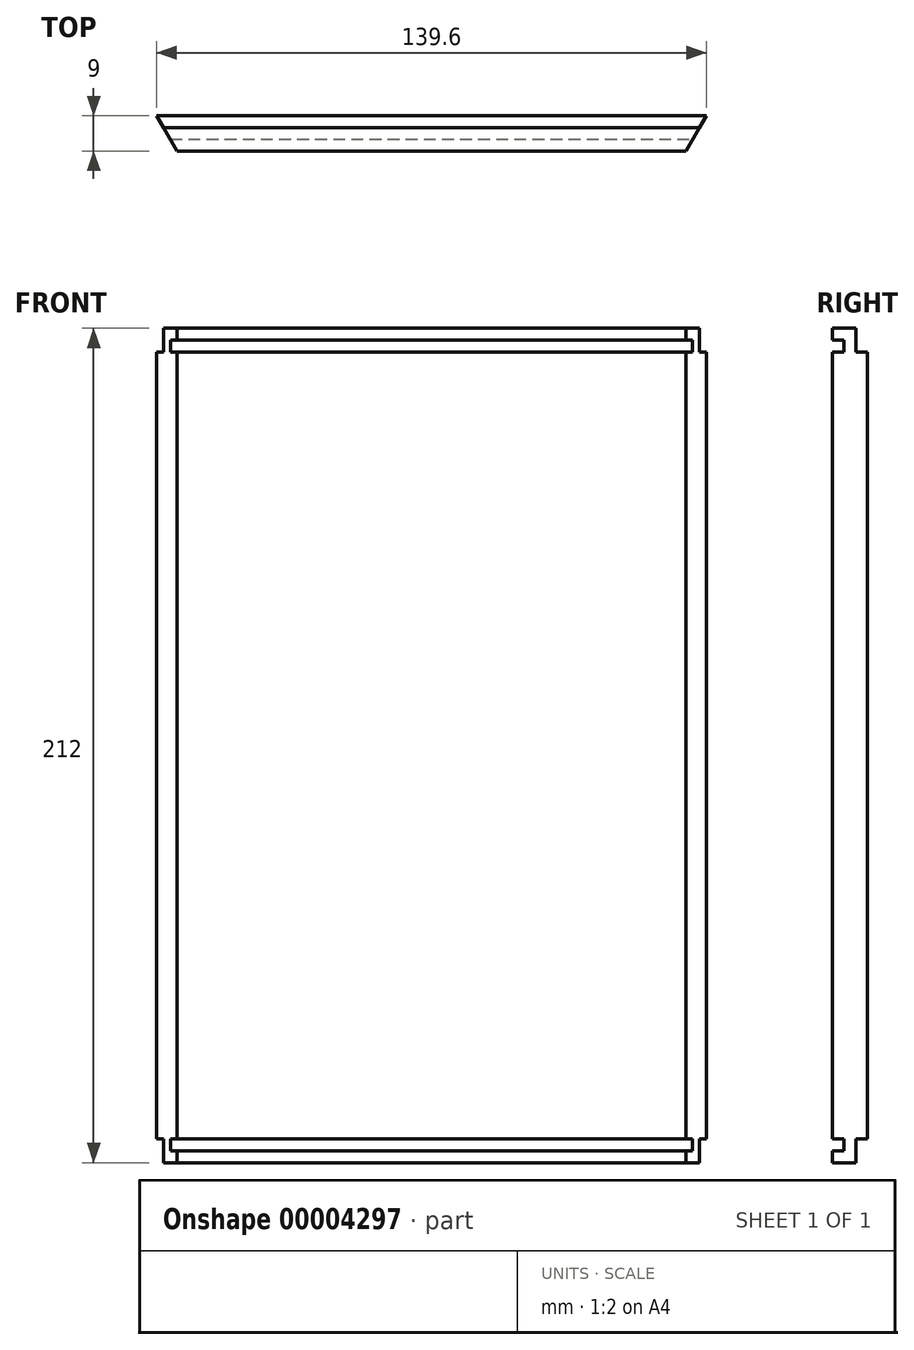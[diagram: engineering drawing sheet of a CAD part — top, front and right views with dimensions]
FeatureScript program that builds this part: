
annotation { "Feature Type Name" : "Feature", "Feature Type Description" : "" }
export const myFeature = defineFeature(function(context is Context, id is Id, definition is map)
    precondition{}
    {
        {
            var Q0;
            Q0=qCreatedBy(makeId("Front.planeOp"),FACE);
            var sketch = newSketch(context, id + "F0", { "sketchPlane" : qUnion([Q0])});
            skLineSegment(sketch, "E0.bottom", {"start": v(-52.97, 148.92) * mm, "end": v(97.03, 148.92) * mm});
            skLineSegment(sketch, "E0.top", {"start": v(-52.97, -51.08) * mm, "end": v(97.03, -51.08) * mm});
            skLineSegment(sketch, "E0.left", {"start": v(-52.97, 148.92) * mm, "end": v(-52.97, -51.08) * mm});
            skLineSegment(sketch, "E0.right", {"start": v(97.03, 148.92) * mm, "end": v(97.03, -51.08) * mm});
            skSolve(sketch);
        }
        {
            var Q0;
            Q0=makeQuery(id+"F0.imprint","IMPRINT",FACE,{"disambiguationData":[TD([[makeQuery(id+"F0.imprint","IMPRINT",EDGE,{"derivedFrom":sQuery(id+"F0.wireOp",EDGE,"E0.bottom")}),-1.0]])]});
            extrude(context, id + "F1", {"entities" : qUnion([Q0]), "depth" : 9 * mm});
        }
        {
            var Q0;
            Q0=makeQuery(id+"F1.opExtrude","SWEPT_FACE",FACE,{"disambiguationData":[OSD([sQuery(id+"F0.wireOp",EDGE,"E0.bottom")])]});
            var sketch = newSketch(context, id + "F2", { "sketchPlane" : qUnion([Q0])});
            skLineSegment(sketch, "E1", {"start": v(-52.97, 0) * mm, "end": v(-52.97, -9) * mm});
            skLineSegment(sketch, "E2", {"start": v(-52.97, -9) * mm, "end": v(97.03, -9) * mm});
            skLineSegment(sketch, "E3", {"start": v(97.03, -9) * mm, "end": v(97.03, 0) * mm});
            skLineSegment(sketch, "E4", {"start": v(97.03, 0) * mm, "end": v(-52.97, 0) * mm});
            skLineSegment(sketch, "E5.0", {"start": v(91.83, -9) * mm, "end": v(91.83, 0) * mm});
            skLineSegment(sketch, "E6", {"start": v(97.03, 0) * mm, "end": v(91.83, -9) * mm});
            skLineSegment(sketch, "E7.0", {"start": v(-46.04, 0) * mm, "end": v(-46.04, -9) * mm});
            skLineSegment(sketch, "E8.0", {"start": v(-40.84, 0) * mm, "end": v(-40.84, -9) * mm});
            skLineSegment(sketch, "E9", {"start": v(-40.84, -9) * mm, "end": v(-46.04, 0) * mm});
            skSolve(sketch);
        }
        {
            var Q0;
            Q0=makeQuery(id+"F1.opExtrude","SWEPT_FACE",FACE,{"disambiguationData":[OSD([sQuery(id+"F0.wireOp",EDGE,"E0.top")])]});
            var sketch = newSketch(context, id + "F3", { "sketchPlane" : qUnion([Q0])});
            skLineSegment(sketch, "E10.0", {"start": v(-52.97, 6) * mm, "end": v(97.03, 6) * mm});
            skLineSegment(sketch, "E11.0", {"start": v(-52.97, 3) * mm, "end": v(97.03, 3) * mm});
            skSolve(sketch);
        }
        {
            var Q0;
            {var subQ3=sQuery(id+"F3.wireOp",EDGE,"E10.0");Q0=makeQuery(id+"F3.imprint","IMPRINT",FACE,{"disambiguationData":[TD([[makeQuery(id+"F3.imprint","IMPRINT",EDGE,{"derivedFrom":subQ3}),-1.0]])]});}
            extrude(context, id + "F4", {"entities" : qUnion([Q0]), "operationType" : NewBodyOperationType.ADD, "depth" : 6 * mm});
        }
        {
            var Q0;
            Q0=makeQuery(id+"F4.opExtrude","SWEPT_FACE",FACE,{"disambiguationData":[OSD([sQuery(id+"F3.wireOp",EDGE,"E10.0")])]});
            var sketch = newSketch(context, id + "F5", { "sketchPlane" : qUnion([Q0])});
            skLineSegment(sketch, "E12.0", {"start": v(-52.97, -54.08) * mm, "end": v(97.03, -54.08) * mm});
            skSolve(sketch);
        }
        {
            var Q0;
            {var subQ3=sQuery(id+"F5.wireOp",EDGE,"E12.0");Q0=makeQuery(id+"F5.imprint","IMPRINT",FACE,{"disambiguationData":[TD([[makeQuery(id+"F5.imprint","IMPRINT",EDGE,{"derivedFrom":subQ3}),-1.0]])]});}
            extrude(context, id + "F6", {"entities" : qUnion([Q0]), "operationType" : NewBodyOperationType.ADD, "depth" : 3 * mm});
        }
        {
            var Q0;
            {var subQ2=sQuery(id+"F2.wireOp",EDGE,"E1");Q0=makeQuery(id+"F2.imprint","IMPRINT",FACE,{"disambiguationData":[TD([[makeQuery(id+"F2.imprint","IMPRINT",EDGE,{"derivedFrom":subQ2}),-1.0]])]});}
            var Q1;
            {var subQ1=sQuery(id+"F2.wireOp",EDGE,"E7.0");Q1=makeQuery(id+"F2.imprint","IMPRINT",FACE,{"disambiguationData":[TD([[makeQuery(id+"F2.imprint","IMPRINT",EDGE,{"derivedFrom":subQ1}),1.0]])]});}
            var Q2;
            {var subQ1=sQuery(id+"F2.wireOp",EDGE,"E3");Q2=makeQuery(id+"F2.imprint","IMPRINT",FACE,{"disambiguationData":[TD([[makeQuery(id+"F2.imprint","IMPRINT",EDGE,{"derivedFrom":subQ1}),1.0]])]});}
            extrude(context, id + "F7", {"entities" : qUnion([Q0, Q1, Q2]), "operationType" : NewBodyOperationType.REMOVE, "oppositeDirection" : true, "depth" : 228.53 * mm});
        }
        {
            var Q0;
            {var subQ0=sQuery(id+"F3.wireOp",EDGE,"E10.0");Q0=makeQuery(id+"F6.boolean.opBoolean","MERGE",FACE,{"derivedFrom":[makeQuery(id+"F4.opExtrude","CAP_FACE",FACE,{"disambiguationData":[OSD([sQuery(id+"F0.wireOp",EDGE,"E0.top"),sQuery(id+"F0.wireOp",EDGE,"E0.left"),sQuery(id+"F0.wireOp",EDGE,"E0.right"),subQ0,sQuery(id+"F3.wireOp",EDGE,"E11.0")])],"isStart":false}),makeQuery(id+"F6.opExtrude","SWEPT_FACE",FACE,{"disambiguationData":[OSD([subQ0])]})]});}
            var sketch = newSketch(context, id + "F8", { "sketchPlane" : qUnion([Q0])});
            skLineSegment(sketch, "E13.0", {"start": v(88.36, 9) * mm, "end": v(91.83, 3) * mm});
            skLineSegment(sketch, "E14", {"start": v(91.83, 9) * mm, "end": v(88.36, 9) * mm});
            skLineSegment(sketch, "E15", {"start": v(95.3, 3) * mm, "end": v(91.83, 3) * mm});
            skLineSegment(sketch, "E16", {"start": v(95.3, 3) * mm, "end": v(91.83, 9) * mm});
            skSolve(sketch);
        }
        {
            var Q0;
            Q0=makeQuery(id+"F8.imprint","IMPRINT",FACE,{"disambiguationData":[TD([[makeQuery(id+"F8.imprint","IMPRINT",EDGE,{"derivedFrom":sQuery(id+"F8.wireOp",EDGE,"E13.0")}),1.0]])]});
            extrude(context, id + "F9", {"entities" : qUnion([Q0]), "operationType" : NewBodyOperationType.REMOVE, "oppositeDirection" : true, "depth" : 3 * mm});
        }
        {
            var Q0;
            Q0=makeQuery(id+"F1.opExtrude","SWEPT_FACE",FACE,{"disambiguationData":[OSD([sQuery(id+"F0.wireOp",EDGE,"E0.bottom")])]});
            var sketch = newSketch(context, id + "F10", { "sketchPlane" : qUnion([Q0])});
            skLineSegment(sketch, "E17.0", {"start": v(-44.3, -3) * mm, "end": v(95.3, -3) * mm});
            skLineSegment(sketch, "E18.0", {"start": v(-42.58, -6) * mm, "end": v(93.56, -6) * mm});
            skLineSegment(sketch, "E19", {"start": v(-46.04, 0) * mm, "end": v(-40.84, -9) * mm});
            skLineSegment(sketch, "E20", {"start": v(97.03, 0) * mm, "end": v(91.83, -9) * mm});
            skSolve(sketch);
        }
        {
            var Q0;
            {var subQ2=sQuery(id+"F10.wireOp",EDGE,"E17.0");Q0=makeQuery(id+"F10.imprint","IMPRINT",FACE,{"disambiguationData":[TD([[makeQuery(id+"F10.imprint","IMPRINT",EDGE,{"derivedFrom":subQ2}),-1.0]])]});}
            extrude(context, id + "F11", {"entities" : qUnion([Q0]), "operationType" : NewBodyOperationType.ADD, "depth" : 6 * mm});
        }
        {
            var Q0;
            Q0=makeQuery(id+"F11.opExtrude","SWEPT_FACE",FACE,{"disambiguationData":[OSD([sQuery(id+"F10.wireOp",EDGE,"E18.0")])]});
            var sketch = newSketch(context, id + "F12", { "sketchPlane" : qUnion([Q0])});
            skLineSegment(sketch, "E21.0", {"start": v(-42.58, 151.92) * mm, "end": v(93.56, 151.92) * mm});
            skSolve(sketch);
        }
        {
            var Q0;
            {var subQ2=sQuery(id+"F12.wireOp",EDGE,"E21.0");Q0=makeQuery(id+"F12.imprint","IMPRINT",FACE,{"disambiguationData":[TD([[makeQuery(id+"F12.imprint","IMPRINT",EDGE,{"derivedFrom":subQ2}),1.0]])]});}
            extrude(context, id + "F13", {"entities" : qUnion([Q0]), "operationType" : NewBodyOperationType.ADD, "depth" : 3 * mm});
        }
        {
            var Q0;
            {var subQ0=sQuery(id+"F10.wireOp",EDGE,"E18.0");Q0=makeQuery(id+"F13.boolean.opBoolean","MERGE",FACE,{"derivedFrom":[makeQuery(id+"F11.opExtrude","CAP_FACE",FACE,{"disambiguationData":[OSD([sQuery(id+"F10.wireOp",EDGE,"E17.0"),subQ0,sQuery(id+"F10.wireOp",EDGE,"E19"),sQuery(id+"F10.wireOp",EDGE,"E20")])],"isStart":false}),makeQuery(id+"F13.opExtrude","SWEPT_FACE",FACE,{"disambiguationData":[OSD([subQ0])]})]});}
            var sketch = newSketch(context, id + "F14", { "sketchPlane" : qUnion([Q0])});
            skLineSegment(sketch, "E22", {"start": v(-44.3, -3) * mm, "end": v(-40.84, -9) * mm});
            skLineSegment(sketch, "E23", {"start": v(-42.58, -9) * mm, "end": v(93.56, -9) * mm});
            skLineSegment(sketch, "E24", {"start": v(93.56, -9) * mm, "end": v(93.56, -6) * mm});
            skLineSegment(sketch, "E25", {"start": v(91.83, -9) * mm, "end": v(95.3, -3) * mm});
            skSolve(sketch);
        }
        {
            var Q0;
            {var subQ1=makeQuery(id+"F13.opExtrude","SWEPT_EDGE",EDGE,{"disambiguationData":[OSD([sQuery(id+"F10.wireOp",EDGE,"E18.0"),sQuery(id+"F10.wireOp",EDGE,"E19")])]});Q0=makeQuery(id+"F14.imprint","IMPRINT",FACE,{"disambiguationData":[TD([[makeQuery(id+"F14.imprint","IMPRINT",EDGE,{"derivedFrom":subQ1}),-1.0]])]});}
            var Q1;
            {var subQ3=sQuery(id+"F14.wireOp",EDGE,"E24");Q1=makeQuery(id+"F14.imprint","IMPRINT",FACE,{"disambiguationData":[TD([[makeQuery(id+"F14.imprint","IMPRINT",EDGE,{"derivedFrom":subQ3}),1.0]])]});}
            extrude(context, id + "F15", {"entities" : qUnion([Q0, Q1]), "operationType" : NewBodyOperationType.REMOVE, "oppositeDirection" : true, "depth" : 3.35 * mm});
        }
        {
            var Q0;
            {var subQ0=sQuery(id+"F10.wireOp",EDGE,"E18.0");Q0=makeQuery(id+"F13.boolean.opBoolean","MERGE",FACE,{"derivedFrom":[makeQuery(id+"F11.opExtrude","CAP_FACE",FACE,{"disambiguationData":[OSD([sQuery(id+"F10.wireOp",EDGE,"E17.0"),subQ0,sQuery(id+"F10.wireOp",EDGE,"E19"),sQuery(id+"F10.wireOp",EDGE,"E20")])],"isStart":false}),makeQuery(id+"F13.opExtrude","SWEPT_FACE",FACE,{"disambiguationData":[OSD([subQ0])]})]});}
            var sketch = newSketch(context, id + "F16", { "sketchPlane" : qUnion([Q0])});
            skLineSegment(sketch, "E26", {"start": v(95.3, -3) * mm, "end": v(91.83, -9) * mm});
            skLineSegment(sketch, "E27", {"start": v(91.83, -9) * mm, "end": v(88.36, -9) * mm});
            skLineSegment(sketch, "E28", {"start": v(95.3, -3) * mm, "end": v(91.83, -3) * mm});
            skLineSegment(sketch, "E29.0", {"start": v(91.83, -3) * mm, "end": v(88.36, -9) * mm});
            skSolve(sketch);
        }
        {
            var Q0;
            Q0=makeQuery(id+"F16.imprint","IMPRINT",FACE,{"disambiguationData":[TD([[makeQuery(id+"F16.imprint","IMPRINT",EDGE,{"derivedFrom":sQuery(id+"F16.wireOp",EDGE,"E26")}),-1.0]])]});
            extrude(context, id + "F17", {"entities" : qUnion([Q0]), "operationType" : NewBodyOperationType.REMOVE, "oppositeDirection" : true, "depth" : 218.46 * mm});
        }
        {
            var Q0;
            {var subQ0=sQuery(id+"F0.wireOp",EDGE,"E0.bottom");Q0=makeQuery(id+"F11.boolean.opBoolean","SPLIT",FACE,{"disambiguationData":[TD([makeQuery(id+"F11.opExtrude","SWEPT_FACE",FACE,{"disambiguationData":[OSD([sQuery(id+"F10.wireOp",EDGE,"E17.0")])]})])],"derivedFrom":makeQuery(id+"F1.opExtrude","SWEPT_FACE",FACE,{"disambiguationData":[OSD([subQ0])]})});}
            var sketch = newSketch(context, id + "F18", { "sketchPlane" : qUnion([Q0])});
            skLineSegment(sketch, "E30.0", {"start": v(93.56, 0) * mm, "end": v(91.83, -3) * mm});
            skLineSegment(sketch, "E31", {"start": v(97.03, 0) * mm, "end": v(93.56, 0) * mm});
            skLineSegment(sketch, "E32", {"start": v(97.03, 0) * mm, "end": v(95.3, -3) * mm});
            skLineSegment(sketch, "E33", {"start": v(91.83, -3) * mm, "end": v(95.3, -3) * mm});
            skSolve(sketch);
        }
        {
            var Q0;
            Q0=makeQuery(id+"F18.imprint","IMPRINT",FACE,{"disambiguationData":[TD([[makeQuery(id+"F18.imprint","IMPRINT",EDGE,{"derivedFrom":sQuery(id+"F18.wireOp",EDGE,"E30.0")}),1.0]])]});
            extrude(context, id + "F19", {"entities" : qUnion([Q0]), "operationType" : NewBodyOperationType.REMOVE, "oppositeDirection" : true, "depth" : 207.75 * mm});
        }
    });
